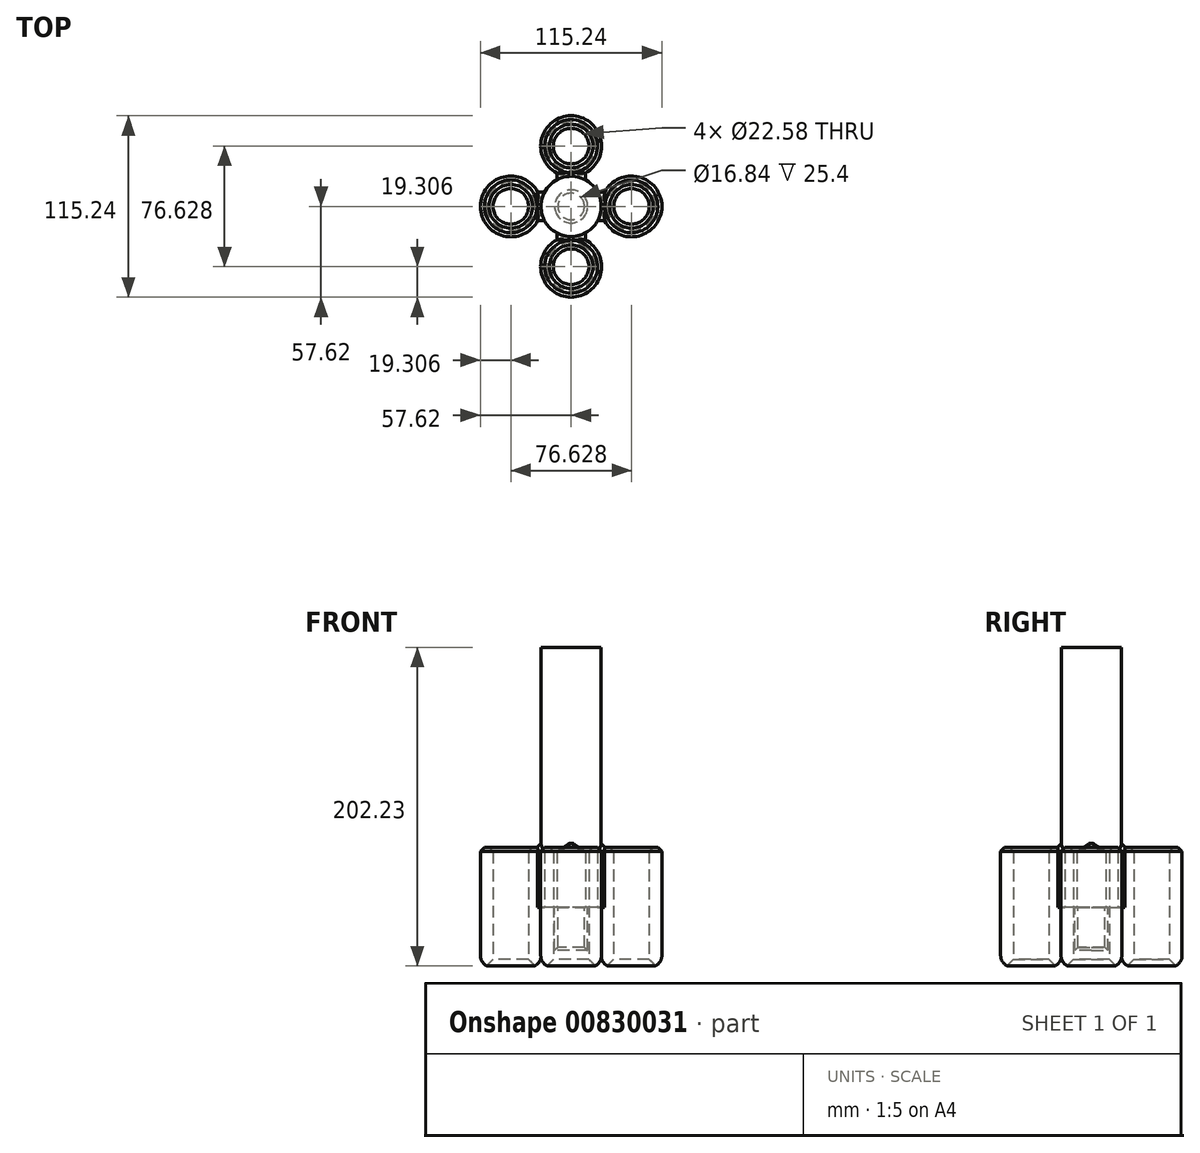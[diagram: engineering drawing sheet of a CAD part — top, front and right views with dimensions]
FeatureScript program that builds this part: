
annotation { "Feature Type Name" : "Feature", "Feature Type Description" : "" }
export const myFeature = defineFeature(function(context is Context, id is Id, definition is map)
    precondition{}
    {
        {
            var Q0;
            Q0=qCreatedBy(makeId("Top.planeOp"),FACE);
            var sketch = newSketch(context, id + "F0", { "sketchPlane" : qUnion([Q0])});
            skCircle(sketch, "E0", {"center": v(0, 0) * mm, "radius": 19.12 * mm});
            skSolve(sketch);
        }
        {
            var Q0;
            Q0=makeQuery(id+"F0.imprint","IMPRINT",FACE,{"disambiguationData":[TD([[makeQuery(id+"F0.imprint","IMPRINT",EDGE,{"derivedFrom":sQuery(id+"F0.wireOp",EDGE,"E0")}),1.0]])]});
            extrude(context, id + "F1", {"entities" : qUnion([Q0]), "depth" : 114.3 * mm, "offsetDistance" : 25.4 * mm});
        }
        {
            var Q0;
            Q0=qCreatedBy(makeId("Top.planeOp"),FACE);
            var sketch = newSketch(context, id + "F2", { "sketchPlane" : qUnion([Q0])});
            skCircle(sketch, "E1", {"center": v(-38.31, 0) * mm, "radius": 19.31 * mm});
            skCircle(sketch, "E2.1.0", {"center": v(0, -38.31) * mm, "radius": 19.31 * mm});
            skCircle(sketch, "E2.2.0", {"center": v(38.31, 0) * mm, "radius": 19.31 * mm});
            skCircle(sketch, "E2.3.0", {"center": v(0, 38.31) * mm, "radius": 19.31 * mm});
            skPoint(sketch, "E2.center", {"position": v(0, 0) * mm});
            skCircle(sketch, "E3", {"center": v(-38.31, 0) * mm, "radius": 11.29 * mm});
            skCircle(sketch, "E4.1.0", {"center": v(0, -38.31) * mm, "radius": 11.29 * mm});
            skCircle(sketch, "E4.2.0", {"center": v(38.31, 0) * mm, "radius": 11.29 * mm});
            skCircle(sketch, "E4.3.0", {"center": v(0, 38.31) * mm, "radius": 11.29 * mm});
            skCircle(sketch, "E5", {"center": v(0, 0) * mm, "radius": 10.5 * mm});
            skCircle(sketch, "E6", {"center": v(0, 0) * mm, "radius": 8.42 * mm});
            skSolve(sketch);
        }
        {
            var Q0;
            Q0=makeQuery(id+"F2.imprint","IMPRINT",FACE,{"disambiguationData":[TD([[makeQuery(id+"F2.imprint","IMPRINT",EDGE,{"derivedFrom":sQuery(id+"F2.wireOp",EDGE,"E2.1.0")}),1.0]])]});
            var Q1;
            Q1=makeQuery(id+"F2.imprint","IMPRINT",FACE,{"disambiguationData":[TD([[makeQuery(id+"F2.imprint","IMPRINT",EDGE,{"derivedFrom":sQuery(id+"F2.wireOp",EDGE,"E2.2.0")}),1.0]])]});
            var Q2;
            Q2=makeQuery(id+"F2.imprint","IMPRINT",FACE,{"disambiguationData":[TD([[makeQuery(id+"F2.imprint","IMPRINT",EDGE,{"derivedFrom":sQuery(id+"F2.wireOp",EDGE,"E2.3.0")}),1.0]])]});
            var Q3;
            Q3=makeQuery(id+"F2.imprint","IMPRINT",FACE,{"disambiguationData":[TD([[makeQuery(id+"F2.imprint","IMPRINT",EDGE,{"derivedFrom":sQuery(id+"F2.wireOp",EDGE,"E1")}),1.0]])]});
            extrude(context, id + "F3", {"entities" : qUnion([Q0, Q1, Q2, Q3]), "operationType" : NewBodyOperationType.ADD, "depth" : 38.1 * mm, "offsetDistance" : 25.4 * mm});
        }
        {
            var Q0;
            Q0 = qSketchRegion(id + "F2", true);
            extrude(context, id + "F4", {"entities" : qUnion([Q0]), "operationType" : NewBodyOperationType.ADD, "depth" : -38.1 * mm, "offsetDistance" : 25.4 * mm});
        }
        {
            var Q0;
            Q0=makeQuery(id+"F4.opExtrude","CAP_EDGE",EDGE,{"disambiguationData":[OSD([sQuery(id+"F2.wireOp",EDGE,"E2.1.0")])],"isStart":false});
            var Q1;
            Q1=makeQuery(id+"F4.opExtrude","CAP_EDGE",EDGE,{"disambiguationData":[OSD([sQuery(id+"F2.wireOp",EDGE,"E2.3.0")])],"isStart":false});
            var Q2;
            Q2=makeQuery(id+"F4.opExtrude","CAP_EDGE",EDGE,{"disambiguationData":[OSD([sQuery(id+"F2.wireOp",EDGE,"E2.2.0")])],"isStart":false});
            var Q3;
            Q3=makeQuery(id+"F4.opExtrude","CAP_EDGE",EDGE,{"disambiguationData":[OSD([sQuery(id+"F2.wireOp",EDGE,"E1")])],"isStart":false});
            fillet(context, id + "F5", {"entities" : qUnion([Q0, Q1, Q2, Q3]), "radius" : 7.62 * mm, "tangentPropagation" : true, "allowEdgeOverflow" : false});
        }
        {
            var Q0;
            Q0=sQuery(id+"F2.wireOp",EDGE,"E4.1.0");
            var Q1;
            Q1=sQuery(id+"F2.wireOp",EDGE,"E4.3.0");
            var Q2;
            Q2=sQuery(id+"F2.wireOp",EDGE,"E3");
            var Q3;
            Q3=sQuery(id+"F2.wireOp",EDGE,"E4.2.0");
            extrude(context, id + "F6", {"bodyType" : ToolBodyType.SURFACE, "surfaceEntities" : qUnion([Q0, Q1, Q2, Q3]), "depth" : 7.62 * mm, "offsetDistance" : 25.4 * mm});
        }
        {
            var Q0;
            Q0=makeQuery(id+"F3.opExtrude","CAP_FACE",FACE,{"disambiguationData":[OSD([sQuery(id+"F2.wireOp",EDGE,"E1"),sQuery(id+"F2.wireOp",EDGE,"E3")])],"isStart":false});
            var Q1;
            Q1=makeQuery(id+"F3.opExtrude","CAP_FACE",FACE,{"disambiguationData":[OSD([sQuery(id+"F2.wireOp",EDGE,"E2.3.0"),sQuery(id+"F2.wireOp",EDGE,"E4.3.0")])],"isStart":false});
            var Q2;
            Q2=makeQuery(id+"F3.opExtrude","CAP_FACE",FACE,{"disambiguationData":[OSD([sQuery(id+"F2.wireOp",EDGE,"E2.2.0"),sQuery(id+"F2.wireOp",EDGE,"E4.2.0")])],"isStart":false});
            var Q3;
            Q3=makeQuery(id+"F3.opExtrude","CAP_FACE",FACE,{"disambiguationData":[OSD([sQuery(id+"F2.wireOp",EDGE,"E2.1.0"),sQuery(id+"F2.wireOp",EDGE,"E4.1.0")])],"isStart":false});
            chamfer(context, id + "F7", {"entities" : qUnion([Q0, Q1, Q2, Q3]), "width" : 2.54 * mm, "tangentPropagation" : true});
        }
        {
            var Q0;
            Q0=makeQuery(id+"F4.opExtrude","CAP_EDGE",EDGE,{"disambiguationData":[OSD([sQuery(id+"F2.wireOp",EDGE,"E4.2.0")])],"isStart":false});
            var Q1;
            Q1=makeQuery(id+"F4.opExtrude","CAP_EDGE",EDGE,{"disambiguationData":[OSD([sQuery(id+"F2.wireOp",EDGE,"E4.1.0")])],"isStart":false});
            var Q2;
            Q2=makeQuery(id+"F4.opExtrude","CAP_EDGE",EDGE,{"disambiguationData":[OSD([sQuery(id+"F2.wireOp",EDGE,"E3")])],"isStart":false});
            var Q3;
            Q3=makeQuery(id+"F4.opExtrude","CAP_EDGE",EDGE,{"disambiguationData":[OSD([sQuery(id+"F2.wireOp",EDGE,"E4.3.0")])],"isStart":false});
            chamfer(context, id + "F8", {"entities" : qUnion([Q0, Q1, Q2, Q3]), "width" : 5.08 * mm, "tangentPropagation" : true});
        }
        {
            var Q0;
            Q0=makeQuery(id+"F4.opExtrude","CAP_FACE",FACE,{"disambiguationData":[OSD([sQuery(id+"F2.wireOp",EDGE,"E5")])],"isStart":false});
            extrude(context, id + "F9", {"entities" : qUnion([Q0]), "operationType" : NewBodyOperationType.ADD, "depth" : -76.2 * mm, "offsetDistance" : 25.4 * mm});
        }
        {
            var Q0;
            Q0=makeQuery(id+"F4.opExtrude","CAP_EDGE",EDGE,{"disambiguationData":[OSD([sQuery(id+"F2.wireOp",EDGE,"E6")])],"isStart":false});
            chamfer(context, id + "F10", {"entities" : qUnion([Q0]), "width" : 12.7 * mm, "tangentPropagation" : true});
        }
        {
            var Q0;
            Q0=makeQuery(id+"F1.opExtrude","CAP_FACE",FACE,{"disambiguationData":[OSD([sQuery(id+"F0.wireOp",EDGE,"E0")])],"isStart":false});
            extrude(context, id + "F11", {"entities" : qUnion([Q0]), "operationType" : NewBodyOperationType.ADD, "depth" : 50.8 * mm, "offsetDistance" : 25.4 * mm});
        }
    });
